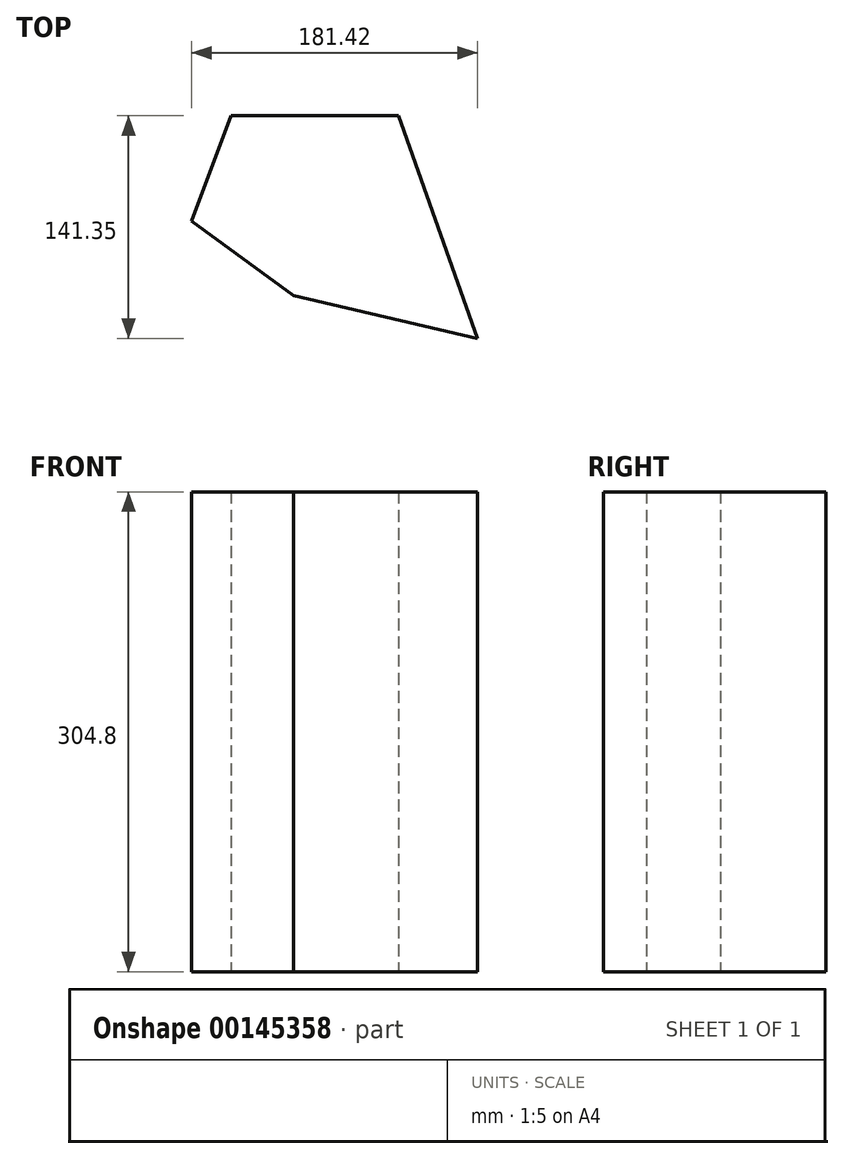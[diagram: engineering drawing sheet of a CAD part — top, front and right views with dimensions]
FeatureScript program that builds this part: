
annotation { "Feature Type Name" : "Feature", "Feature Type Description" : "" }
export const myFeature = defineFeature(function(context is Context, id is Id, definition is map)
    precondition{}
    {
        {
            var Q0;
            Q0=qCreatedBy(makeId("Top.planeOp"),FACE);
            var sketch = newSketch(context, id + "F0", { "sketchPlane" : qUnion([Q0])});
            skLineSegment(sketch, "E0", {"start": v(-58.07, -8.84) * mm, "end": v(-32.9, 58) * mm});
            skLineSegment(sketch, "E1", {"start": v(-32.9, 58) * mm, "end": v(73.3, 58) * mm});
            skLineSegment(sketch, "E2", {"start": v(73.3, 58) * mm, "end": v(123.35, -83.35) * mm});
            skLineSegment(sketch, "E3", {"start": v(123.35, -83.35) * mm, "end": v(6.78, -56.03) * mm});
            skLineSegment(sketch, "E4", {"start": v(6.78, -56.03) * mm, "end": v(-58.07, -8.84) * mm});
            skSolve(sketch);
        }
        {
            var Q0;
            Q0 = qSketchRegion(id + "F0", true);
            extrude(context, id + "F1", {"entities" : qUnion([Q0]), "endBound" : BoundingType.SYMMETRIC, "depth" : 304.8 * mm});
        }
    });
